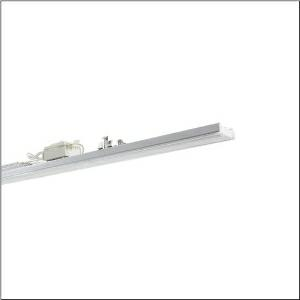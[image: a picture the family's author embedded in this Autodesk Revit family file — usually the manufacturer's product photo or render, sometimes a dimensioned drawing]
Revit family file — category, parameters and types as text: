
# Revit family: licross_r__21_recessed_ho_52tl12dv4l2m3s_7bf3
name_source: partatom
category: Lighting Fixtures
units: mm (PartAtom-declared; Revit-internal decimal feet)

## family parameters
Cut with Voids When Loaded = No
Host = Face
Light Source = No
Part Type = Normal
Room Calculation Point = No
Round Connector Dimension = Use Diameter
Shared = No

## types (1)
- --- (1 x LED, 910 lm, 6.4 W, 4000K)
    Apparent Load = 6 VA
    CIE Flux Codes = 69 91 98 100 100
    Color Rendering = 80
    Color Temperature = 4000K
    Default Elevation = 1800 mm
    Description = Licross® 21 Recessed HO, luminaire insert, of sheet steel, galvanised, coil coated, white, length: 2.250mm, width: 66mm, height: 67mm, LED rated luminous flux: 22.710lm, light colour: 840, control gear: DALI 2 (for two DALI lines), with plug, 6-pole, with phase selection, for trunking rail, 14-core, mains connection: 220..240V, AC, 50/60Hz, rated input power: 129W, for trunking rail, 14-core, halogen-free wiring, for emergency light function, converter,control gear: single battery element, battery: LiFePO4, 9Ah, primary optical cover: cover, of PMMA, light emission: direct distribution, primary light characteristic: symmetric, protection rating (complete): IP40, insulation class (complete): insulation class I (protective earthing), certification: CE, UKCA, protection symbol: D if used in an environment without relevant dust loads with corresponding accessories, impact resistance: IK06, permissible ambient temperature for indoor applications: +5..+30°C, standard: EN 60598-2-22, LABS conformity tested according to VDMA 24364:2018-05, reducing of maximum allowable ambient temperature of 5°C with ceiling mounting, corresponds to IFS (International Featured Standards) requirements for safety and quality in the food industry, packaging unit: 1 piece
    Height = 58 mm
    Lamp = 1 x LED
    Lamp Light Flux = 910 lm
    Lamp Power = 6.4 W
    Lamp count = 1
    Length = 2250 mm
    Luminous efficacy = 142 lm/W
    Manufacturer = Siteco
    ModVariant = No
    Model = 52TL12DV4L2M3S
    Mounting Place = Ceiling
    Mounting Type = Pendant
    Number of Poles = 1
    OnlyDefault = Yes
    Power Factor = 1
    Product Name = Licross® 21 Recessed HO
    Product group = luminaire insert
    ProductGroupID = 902
    Protection Class = Protection class I
    Protection Degree = IP 40
    RLX_Detail_Level = 1
    RLX_Emergency_Light_Flux = 0 lm
    RLX_Emergency_Type = 0
    RLX_Emergency_Type_DB = No
    RlxData = <blob elided: 29985 chars, md5=aca59549>
    Socket = socket
    Standby Power = 0 W
    System Light Flux = 910 lm
    System Power = 6 W
    Type Comments = : emergency light operation: 3 h
    Type Image = l_1296930.jpg
    URL = http://relux.com
    VarID = @adj_109336
    Voltage = 0 V
    Weight = 0.00 kg
    Width = 66 mm

## geometry (parser evidence)
native form markers: Blend x4, Sweep x9
no freeform markers — native parametric forms only
